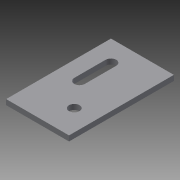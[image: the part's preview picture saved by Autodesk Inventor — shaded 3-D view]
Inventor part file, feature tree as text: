
AUTODESK INVENTOR PART (.ipt)
format: ipt  version: 2015 (Build 190159000, 159)  size: 87,040 bytes
history: native  units: in
note: dims shown in document units (in); Inventor stores cm internally (conversion verified against a paired STEP export)
features: extrude x1, sketch x1
ambient origin geometry x8: Origin, YZ Plane, XZ Plane, XY Plane, X Axis, Y Axis, Z Axis, Center Point
bodies: Solid1 (feature_tree)
feature tree (2):
  extrude  "Extrusion1"  Depth=2.5in
  sketch  "Sketch1"  dims[d0=1.5in d2=2.5in d3=0.75in d4=2.0in d5=0.5in d6=0.625in d7=1.0in d8=0.125in d9=0.0in d10=0.125in d11=0.125in d12=0.25in]
